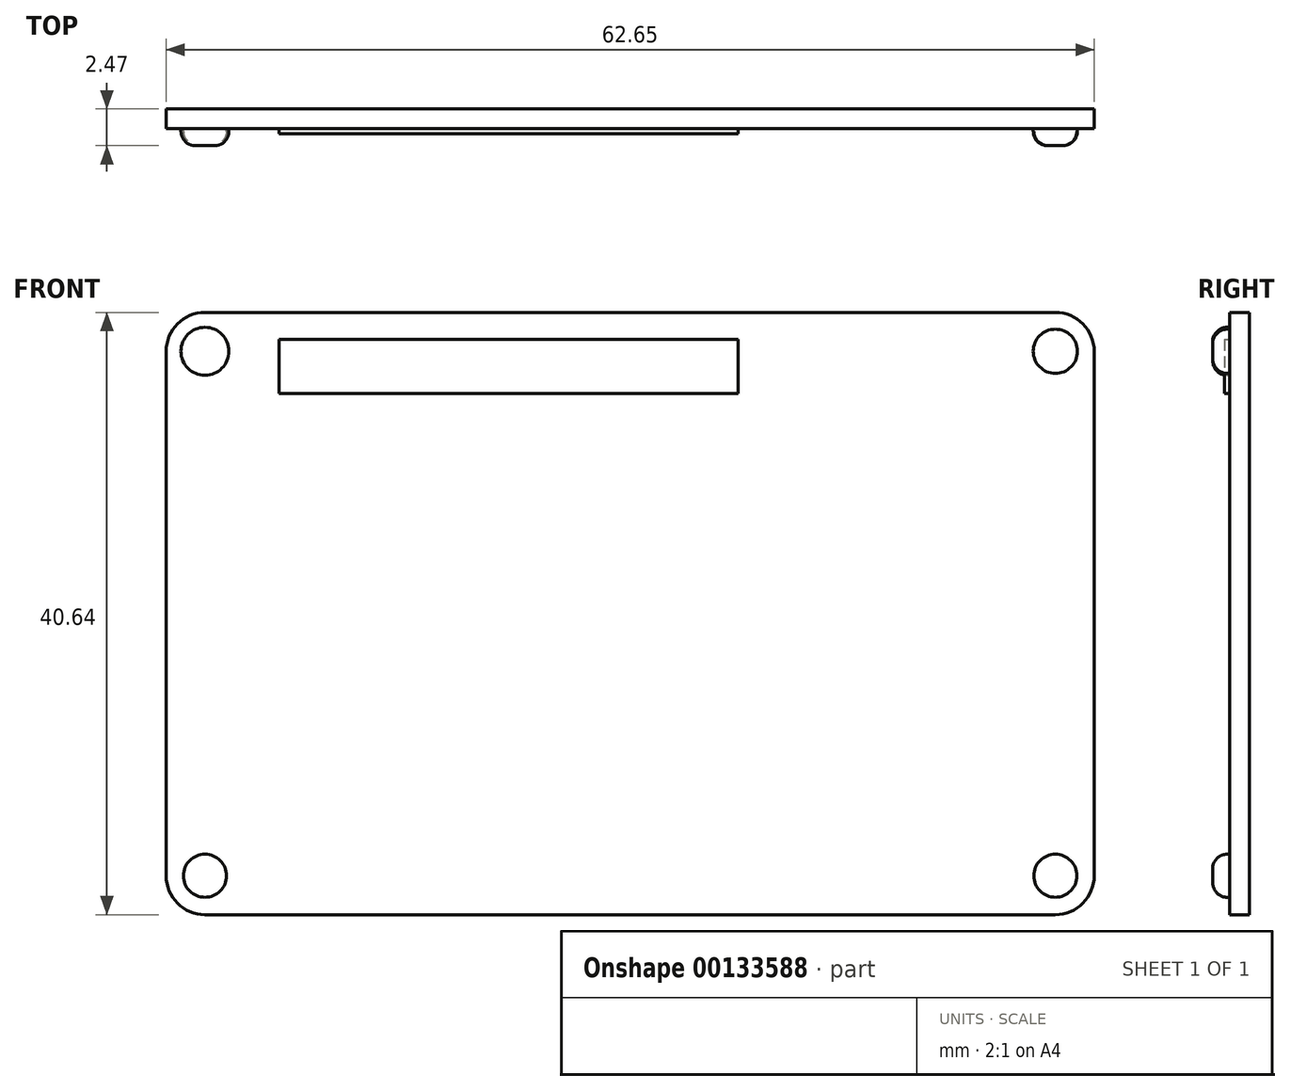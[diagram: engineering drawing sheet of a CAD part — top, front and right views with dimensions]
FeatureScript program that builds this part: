
annotation { "Feature Type Name" : "Feature", "Feature Type Description" : "" }
export const myFeature = defineFeature(function(context is Context, id is Id, definition is map)
    precondition{}
    {
        {
            var Q0;
            Q0=qCreatedBy(makeId("Front.planeOp"),FACE);
            var sketch = newSketch(context, id + "F0", { "sketchPlane" : qUnion([Q0])});
            skLineSegment(sketch, "E0.bottom", {"start": v(-62.65, 61.79) * mm, "end": v(0, 61.79) * mm});
            skLineSegment(sketch, "E0.top", {"start": v(-62.65, 21.15) * mm, "end": v(0, 21.15) * mm});
            skLineSegment(sketch, "E0.left", {"start": v(-62.65, 61.79) * mm, "end": v(-62.65, 21.15) * mm});
            skLineSegment(sketch, "E0.right", {"start": v(0, 61.79) * mm, "end": v(0, 21.15) * mm});
            skSolve(sketch);
        }
        {
            var Q0;
            Q0=makeQuery(id+"F0.imprint","IMPRINT",FACE,{"disambiguationData":[TD([[makeQuery(id+"F0.imprint","IMPRINT",EDGE,{"derivedFrom":sQuery(id+"F0.wireOp",EDGE,"E0.bottom")}),-1.0]])]});
            extrude(context, id + "F6", {"entities" : qUnion([Q0]), "depth" : 1.33 * mm});
        }
        {
            var Q0;
            Q0=makeQuery(id+"F6.opExtrude","SWEPT_EDGE",EDGE,{"disambiguationData":[OSD([sQuery(id+"F0.wireOp",EDGE,"E0.top"),sQuery(id+"F0.wireOp",EDGE,"E0.left")])]});
            var Q1;
            Q1=makeQuery(id+"F6.opExtrude","SWEPT_EDGE",EDGE,{"disambiguationData":[OSD([sQuery(id+"F0.wireOp",EDGE,"E0.bottom"),sQuery(id+"F0.wireOp",EDGE,"E0.left")])]});
            var Q2;
            Q2=makeQuery(id+"F6.opExtrude","SWEPT_EDGE",EDGE,{"disambiguationData":[OSD([sQuery(id+"F0.wireOp",EDGE,"E0.bottom"),sQuery(id+"F0.wireOp",EDGE,"E0.right")])]});
            var Q3;
            Q3=makeQuery(id+"F6.opExtrude","SWEPT_EDGE",EDGE,{"disambiguationData":[OSD([sQuery(id+"F0.wireOp",EDGE,"E0.top"),sQuery(id+"F0.wireOp",EDGE,"E0.right")])]});
            fillet(context, id + "F1", {"entities" : qUnion([Q0, Q1, Q2, Q3]), "radius" : 2.62 * mm, "tangentPropagation" : true, "allowEdgeOverflow" : false});
        }
        {
            var Q0;
            Q0=makeQuery(id+"F6.opExtrude","CAP_FACE",FACE,{"disambiguationData":[OSD([sQuery(id+"F0.wireOp",EDGE,"E0.bottom"),sQuery(id+"F0.wireOp",EDGE,"E0.top"),sQuery(id+"F0.wireOp",EDGE,"E0.left"),sQuery(id+"F0.wireOp",EDGE,"E0.right")])],"isStart":false});
            var sketch = newSketch(context, id + "F2", { "sketchPlane" : qUnion([Q0])});
            skCircle(sketch, "E1", {"center": v(-2.62, 59.16) * mm, "radius": 1.5 * mm});
            skCircle(sketch, "E2", {"center": v(-2.62, 23.77) * mm, "radius": 1.45 * mm});
            skCircle(sketch, "E3", {"center": v(-60.03, 59.16) * mm, "radius": 1.62 * mm});
            skCircle(sketch, "E4", {"center": v(-60.03, 23.77) * mm, "radius": 1.45 * mm});
            skSolve(sketch);
        }
        {
            var Q0;
            Q0=makeQuery(id+"F2.imprint","IMPRINT",FACE,{"disambiguationData":[TD([[makeQuery(id+"F2.imprint","IMPRINT",EDGE,{"derivedFrom":sQuery(id+"F2.wireOp",EDGE,"E1")}),1.0]])]});
            var Q1;
            Q1=makeQuery(id+"F2.imprint","IMPRINT",FACE,{"disambiguationData":[TD([[makeQuery(id+"F2.imprint","IMPRINT",EDGE,{"derivedFrom":sQuery(id+"F2.wireOp",EDGE,"E4")}),1.0]])]});
            var Q2;
            Q2=makeQuery(id+"F2.imprint","IMPRINT",FACE,{"disambiguationData":[TD([[makeQuery(id+"F2.imprint","IMPRINT",EDGE,{"derivedFrom":sQuery(id+"F2.wireOp",EDGE,"E3")}),1.0]])]});
            var Q3;
            Q3=makeQuery(id+"F2.imprint","IMPRINT",FACE,{"disambiguationData":[TD([[makeQuery(id+"F2.imprint","IMPRINT",EDGE,{"derivedFrom":sQuery(id+"F2.wireOp",EDGE,"E2")}),1.0]])]});
            extrude(context, id + "F3", {"entities" : qUnion([Q0, Q1, Q2, Q3]), "operationType" : NewBodyOperationType.ADD, "depth" : 1.13 * mm});
        }
        {
            var Q0;
            Q0=makeQuery(id+"F3.opExtrude","CAP_EDGE",EDGE,{"disambiguationData":[OSD([sQuery(id+"F2.wireOp",EDGE,"E2")])],"isStart":false});
            var Q1;
            Q1=makeQuery(id+"F3.opExtrude","CAP_EDGE",EDGE,{"disambiguationData":[OSD([sQuery(id+"F2.wireOp",EDGE,"E1")])],"isStart":false});
            var Q2;
            Q2=makeQuery(id+"F3.opExtrude","CAP_EDGE",EDGE,{"disambiguationData":[OSD([sQuery(id+"F2.wireOp",EDGE,"E4")])],"isStart":false});
            var Q3;
            Q3=makeQuery(id+"F3.opExtrude","CAP_EDGE",EDGE,{"disambiguationData":[OSD([sQuery(id+"F2.wireOp",EDGE,"E3")])],"isStart":false});
            fillet(context, id + "F4", {"entities" : qUnion([Q0, Q1, Q2, Q3]), "radius" : 0.97 * mm, "tangentPropagation" : true, "allowEdgeOverflow" : false});
        }
        {
            var Q0;
            Q0=makeQuery(id+"F6.opExtrude","CAP_FACE",FACE,{"disambiguationData":[OSD([sQuery(id+"F0.wireOp",EDGE,"E0.bottom"),sQuery(id+"F0.wireOp",EDGE,"E0.top"),sQuery(id+"F0.wireOp",EDGE,"E0.left"),sQuery(id+"F0.wireOp",EDGE,"E0.right")])],"isStart":false});
            var sketch = newSketch(context, id + "F5", { "sketchPlane" : qUnion([Q0])});
            skLineSegment(sketch, "E5.bottom", {"start": v(-55.02, 59.97) * mm, "end": v(-24.05, 59.97) * mm});
            skLineSegment(sketch, "E5.top", {"start": v(-55.02, 56.32) * mm, "end": v(-24.05, 56.32) * mm});
            skLineSegment(sketch, "E5.left", {"start": v(-55.02, 59.97) * mm, "end": v(-55.02, 56.32) * mm});
            skLineSegment(sketch, "E5.right", {"start": v(-24.05, 59.97) * mm, "end": v(-24.05, 56.32) * mm});
            skSolve(sketch);
        }
        {
            var Q0;
            Q0=makeQuery(id+"F5.imprint","IMPRINT",FACE,{"disambiguationData":[TD([[makeQuery(id+"F5.imprint","IMPRINT",EDGE,{"derivedFrom":sQuery(id+"F5.wireOp",EDGE,"E5.bottom")}),-1.0]])]});
            extrude(context, id + "F7", {"entities" : qUnion([Q0]), "operationType" : NewBodyOperationType.ADD, "depth" : 0.34 * mm});
        }
    });
